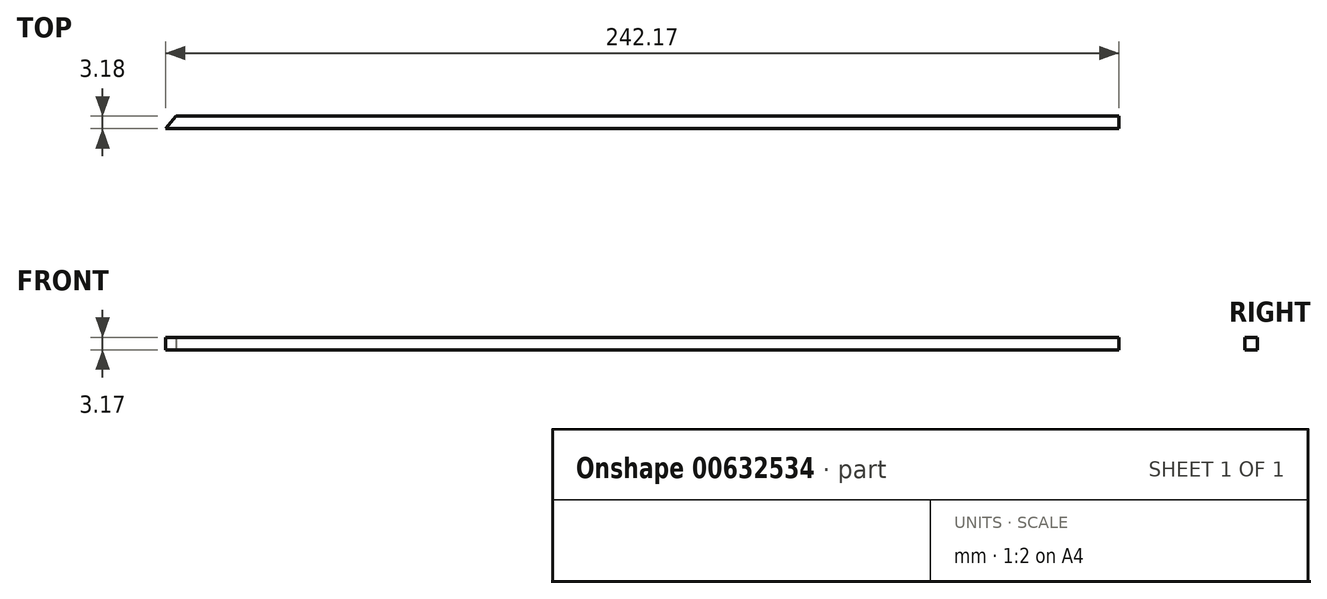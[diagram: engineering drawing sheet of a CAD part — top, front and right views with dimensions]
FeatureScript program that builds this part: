
annotation { "Feature Type Name" : "Feature", "Feature Type Description" : "" }
export const myFeature = defineFeature(function(context is Context, id is Id, definition is map)
    precondition{}
    {
        {
            var Q0;
            Q0=qCreatedBy(makeId("Top.planeOp"),FACE);
            var sketch = newSketch(context, id + "F0", { "sketchPlane" : qUnion([Q0])});
            skLineSegment(sketch, "E0", {"start": v(-153, 3.17) * mm, "end": v(86.52, 3.17) * mm});
            skLineSegment(sketch, "E1", {"start": v(86.52, 3.17) * mm, "end": v(86.52, 0) * mm});
            skLineSegment(sketch, "E2", {"start": v(86.52, 0) * mm, "end": v(-155.65, 0) * mm});
            skLineSegment(sketch, "E3", {"start": v(-155.65, 0) * mm, "end": v(-153, 3.17) * mm});
            skSolve(sketch);
        }
        {
            var Q0;
            Q0=makeQuery(id+"F0.imprint","IMPRINT",FACE,{"disambiguationData":[TD([[makeQuery(id+"F0.imprint","IMPRINT",EDGE,{"derivedFrom":sQuery(id+"F0.wireOp",EDGE,"E0")}),-1.0]])]});
            extrude(context, id + "F1", {"entities" : qUnion([Q0]), "depth" : 3.17 * mm, "offsetDistance" : 25.4 * mm});
        }
    });
